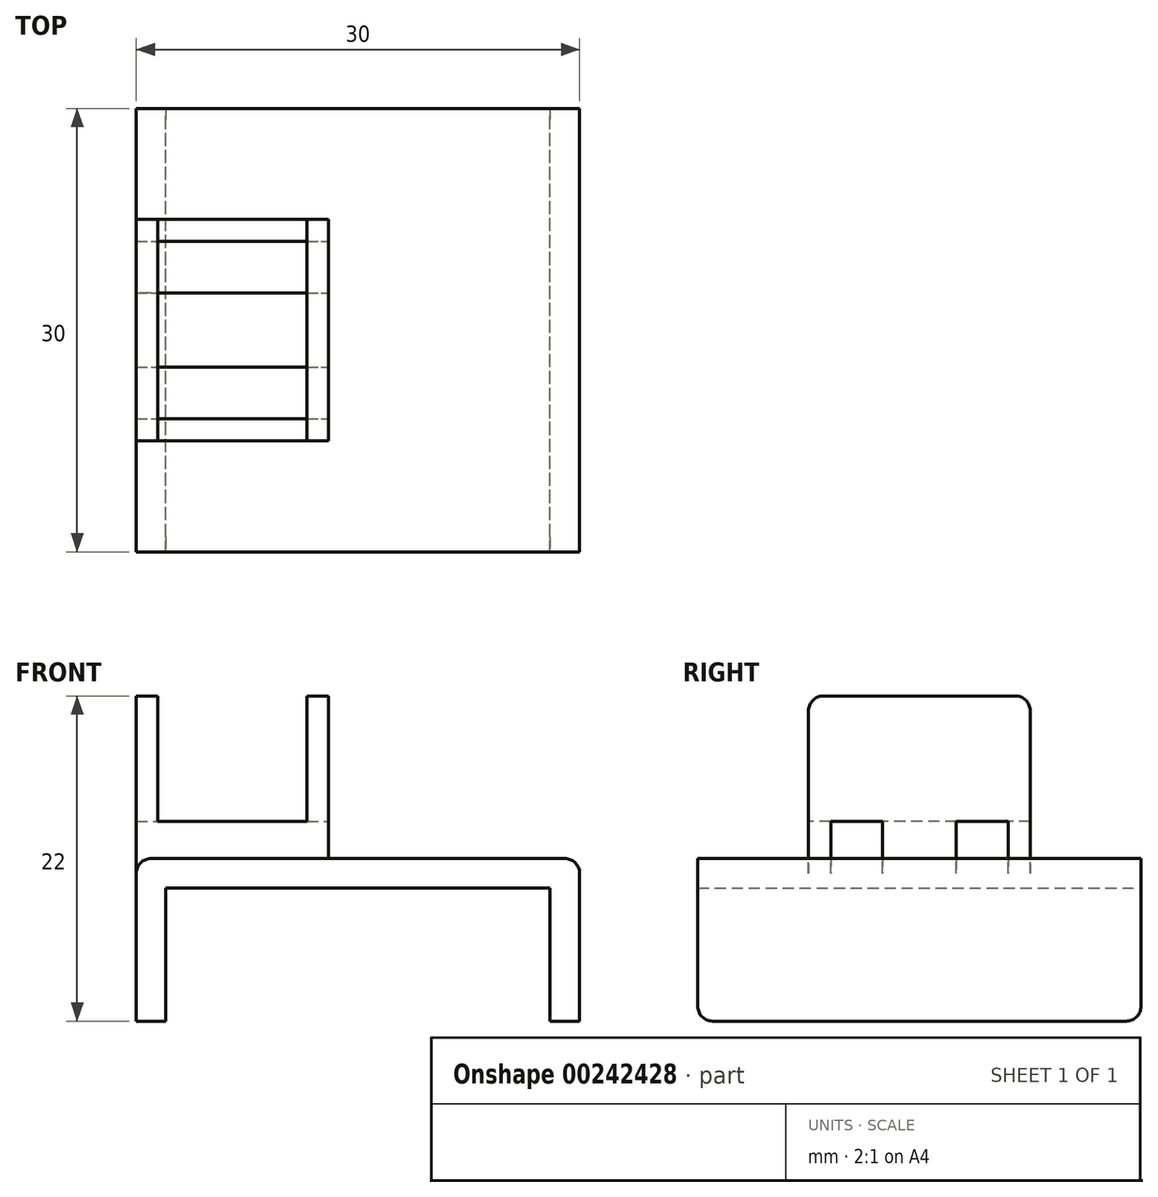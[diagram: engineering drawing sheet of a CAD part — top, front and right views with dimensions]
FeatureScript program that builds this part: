
annotation { "Feature Type Name" : "Feature", "Feature Type Description" : "" }
export const myFeature = defineFeature(function(context is Context, id is Id, definition is map)
    precondition{}
    {
        {
            var Q0;
            Q0=qCreatedBy(makeId("Top.planeOp"),FACE);
            var sketch = newSketch(context, id + "F0", { "sketchPlane" : qUnion([Q0])});
            skLineSegment(sketch, "E0.bottom", {"start": v(15, -15) * mm, "end": v(-15, -15) * mm});
            skLineSegment(sketch, "E0.top", {"start": v(15, 15) * mm, "end": v(-15, 15) * mm});
            skLineSegment(sketch, "E0.left", {"start": v(15, -15) * mm, "end": v(15, 15) * mm});
            skLineSegment(sketch, "E0.right", {"start": v(-15, -15) * mm, "end": v(-15, 15) * mm});
            skPoint(sketch, "E0.middle", {"position": v(0, 0) * mm});
            skSolve(sketch);
        }
        {
            var Q0;
            Q0=makeQuery(id+"F0.imprint","IMPRINT",FACE,{"disambiguationData":[TD([[makeQuery(id+"F0.imprint","IMPRINT",EDGE,{"derivedFrom":sQuery(id+"F0.wireOp",EDGE,"E0.bottom")}),-1.0]])]});
            extrude(context, id + "F1", {"entities" : qUnion([Q0]), "depth" : 11 * mm, "offsetDistance" : 25 * mm});
        }
        {
            var Q0;
            Q0=makeQuery(id+"F1.opExtrude","CAP_FACE",FACE,{"disambiguationData":[OSD([sQuery(id+"F0.wireOp",EDGE,"E0.bottom"),sQuery(id+"F0.wireOp",EDGE,"E0.top"),sQuery(id+"F0.wireOp",EDGE,"E0.left"),sQuery(id+"F0.wireOp",EDGE,"E0.right")])],"isStart":true});
            var sketch = newSketch(context, id + "F2", { "sketchPlane" : qUnion([Q0])});
            skLineSegment(sketch, "E1", {"start": v(-13, 15) * mm, "end": v(-13, -15) * mm});
            skLineSegment(sketch, "E2", {"start": v(13, 15) * mm, "end": v(13, -15) * mm});
            skLineSegment(sketch, "E3", {"start": v(0, -19.21) * mm, "end": v(0, -15) * mm, "construction": true});
            skSolve(sketch);
        }
        {
            var Q0;
            {var subQ0=sQuery(id+"F2.wireOp",EDGE,"E1");Q0=makeQuery(id+"F2.imprint","IMPRINT",FACE,{"disambiguationData":[TD([[makeQuery(id+"F2.imprint","IMPRINT",EDGE,{"derivedFrom":subQ0}),1.0]])]});}
            extrude(context, id + "F3", {"entities" : qUnion([Q0]), "operationType" : NewBodyOperationType.REMOVE, "oppositeDirection" : true, "depth" : 9 * mm, "offsetDistance" : 25 * mm});
        }
        {
            var Q0;
            Q0=makeQuery(id+"F1.opExtrude","CAP_FACE",FACE,{"disambiguationData":[OSD([sQuery(id+"F0.wireOp",EDGE,"E0.bottom"),sQuery(id+"F0.wireOp",EDGE,"E0.top"),sQuery(id+"F0.wireOp",EDGE,"E0.left"),sQuery(id+"F0.wireOp",EDGE,"E0.right")])],"isStart":false});
            var sketch = newSketch(context, id + "F4", { "sketchPlane" : qUnion([Q0])});
            skLineSegment(sketch, "E4", {"start": v(-2, 15) * mm, "end": v(-2, -15) * mm});
            skLineSegment(sketch, "E5", {"start": v(-13.55, 15) * mm, "end": v(-13.55, -15) * mm});
            skLineSegment(sketch, "E6", {"start": v(-3.45, 15) * mm, "end": v(-3.45, -15) * mm});
            skLineSegment(sketch, "E7", {"start": v(-15, 7.5) * mm, "end": v(-13.55, 7.5) * mm});
            skLineSegment(sketch, "E8", {"start": v(-15, -7.5) * mm, "end": v(-13.55, -7.5) * mm});
            skLineSegment(sketch, "E9", {"start": v(-3.45, 7.5) * mm, "end": v(-2, 7.5) * mm});
            skLineSegment(sketch, "E10", {"start": v(-3.45, -7.5) * mm, "end": v(-2, -7.5) * mm});
            skLineSegment(sketch, "E11", {"start": v(-15, 0) * mm, "end": v(-7.7, 0) * mm, "construction": true});
            skSolve(sketch);
        }
        {
            var Q0;
            {var subQ0=sQuery(id+"F4.wireOp",EDGE,"E7");Q0=makeQuery(id+"F4.imprint","IMPRINT",FACE,{"disambiguationData":[TD([[makeQuery(id+"F4.imprint","IMPRINT",EDGE,{"derivedFrom":subQ0}),-1.0]])]});}
            var Q1;
            {var subQ0=sQuery(id+"F4.wireOp",EDGE,"E9");Q1=makeQuery(id+"F4.imprint","IMPRINT",FACE,{"disambiguationData":[TD([[makeQuery(id+"F4.imprint","IMPRINT",EDGE,{"derivedFrom":subQ0}),-1.0]])]});}
            extrude(context, id + "F5", {"entities" : qUnion([Q0, Q1]), "operationType" : NewBodyOperationType.ADD, "depth" : 11 * mm, "offsetDistance" : 25 * mm});
        }
        {
            var Q0;
            Q0=makeQuery(id+"F1.opExtrude","CAP_FACE",FACE,{"disambiguationData":[OSD([sQuery(id+"F0.wireOp",EDGE,"E0.bottom"),sQuery(id+"F0.wireOp",EDGE,"E0.top"),sQuery(id+"F0.wireOp",EDGE,"E0.left"),sQuery(id+"F0.wireOp",EDGE,"E0.right")])],"isStart":false});
            var sketch = newSketch(context, id + "F6", { "sketchPlane" : qUnion([Q0])});
            skLineSegment(sketch, "E12", {"start": v(-13.55, 7.5) * mm, "end": v(-3.45, 7.5) * mm});
            skLineSegment(sketch, "E13", {"start": v(-13.55, -7.5) * mm, "end": v(-3.45, -7.5) * mm});
            skSolve(sketch);
        }
        {
            var Q0;
            Q0=makeQuery(id+"F6.imprint","IMPRINT",FACE,{"disambiguationData":[TD([[makeQuery(id+"F6.imprint","IMPRINT",EDGE,{"derivedFrom":sQuery(id+"F6.wireOp",EDGE,"E12")}),-1.0]])]});
            extrude(context, id + "F7", {"entities" : qUnion([Q0]), "operationType" : NewBodyOperationType.ADD, "depth" : 2.5 * mm, "offsetDistance" : 25 * mm});
        }
        {
            var Q0;
            Q0=makeQuery(id+"F5.opExtrude","SWEPT_FACE",FACE,{"disambiguationData":[OSD([sQuery(id+"F4.wireOp",EDGE,"E4")])]});
            var sketch = newSketch(context, id + "F8", { "sketchPlane" : qUnion([Q0])});
            skLineSegment(sketch, "E14.bottom", {"start": v(6, 13.5) * mm, "end": v(2.5, 13.5) * mm});
            skLineSegment(sketch, "E14.top", {"start": v(6, 11) * mm, "end": v(2.5, 11) * mm});
            skLineSegment(sketch, "E14.left", {"start": v(6, 11) * mm, "end": v(6, 13.5) * mm});
            skLineSegment(sketch, "E14.right", {"start": v(2.5, 13.5) * mm, "end": v(2.5, 11) * mm});
            skPoint(sketch, "E14.middle", {"position": v(4.25, 12.25) * mm});
            skLineSegment(sketch, "E15.bottom", {"start": v(-2.5, 11) * mm, "end": v(-6, 11) * mm});
            skLineSegment(sketch, "E15.top", {"start": v(-2.5, 13.5) * mm, "end": v(-6, 13.5) * mm});
            skLineSegment(sketch, "E15.left", {"start": v(-2.5, 11) * mm, "end": v(-2.5, 13.5) * mm});
            skLineSegment(sketch, "E15.right", {"start": v(-6, 11) * mm, "end": v(-6, 13.5) * mm});
            skPoint(sketch, "E15.middle", {"position": v(-4.25, 12.25) * mm});
            skLineSegment(sketch, "E16", {"start": v(0, 11) * mm, "end": v(0, 18.6) * mm, "construction": true});
            skSolve(sketch);
        }
        {
            var Q0;
            Q0=makeQuery(id+"F8.imprint","IMPRINT",FACE,{"disambiguationData":[TD([[makeQuery(id+"F8.imprint","IMPRINT",EDGE,{"derivedFrom":sQuery(id+"F8.wireOp",EDGE,"E15.bottom")}),-1.0]])]});
            var Q1;
            Q1=makeQuery(id+"F8.imprint","IMPRINT",FACE,{"disambiguationData":[TD([[makeQuery(id+"F8.imprint","IMPRINT",EDGE,{"derivedFrom":sQuery(id+"F8.wireOp",EDGE,"E14.bottom")}),1.0]])]});
            extrude(context, id + "F9", {"entities" : qUnion([Q0, Q1]), "operationType" : NewBodyOperationType.REMOVE, "endBound" : BoundingType.THROUGH_ALL, "oppositeDirection" : true, "depth" : 25 * mm, "offsetDistance" : 25 * mm});
        }
        {
            var Q0;
            Q0=makeQuery(id+"F5.opExtrude","CAP_EDGE",EDGE,{"disambiguationData":[OSD([sQuery(id+"F4.wireOp",EDGE,"E7")])],"isStart":false});
            var Q1;
            Q1=makeQuery(id+"F5.opExtrude","CAP_EDGE",EDGE,{"disambiguationData":[OSD([sQuery(id+"F4.wireOp",EDGE,"E8")])],"isStart":false});
            var Q2;
            Q2=makeQuery(id+"F5.opExtrude","CAP_EDGE",EDGE,{"disambiguationData":[OSD([sQuery(id+"F4.wireOp",EDGE,"E10")])],"isStart":false});
            var Q3;
            Q3=makeQuery(id+"F5.opExtrude","CAP_EDGE",EDGE,{"disambiguationData":[OSD([sQuery(id+"F4.wireOp",EDGE,"E9")])],"isStart":false});
            var Q4;
            {var subQ0=sQuery(id+"F0.wireOp",EDGE,"E0.right");var subQ1=sQuery(id+"F0.wireOp",EDGE,"E0.bottom");Q4=makeQuery(id+"F5.boolean.opBoolean","SPLIT",EDGE,{"disambiguationData":[TD([makeQuery(id+"F1.opExtrude","SWEPT_FACE",FACE,{"disambiguationData":[OSD([subQ1])]})])],"derivedFrom":makeQuery(id+"F1.opExtrude","CAP_EDGE",EDGE,{"disambiguationData":[OSD([subQ0])],"isStart":false})});}
            var Q5;
            Q5=makeQuery(id+"F1.opExtrude","CAP_EDGE",EDGE,{"disambiguationData":[OSD([sQuery(id+"F0.wireOp",EDGE,"E0.left")])],"isStart":false});
            var Q6;
            {var subQ0=sQuery(id+"F0.wireOp",EDGE,"E0.bottom");var subQ1=sQuery(id+"F0.wireOp",EDGE,"E0.right");Q6=makeQuery(id+"F3.boolean.opBoolean","SPLIT",EDGE,{"disambiguationData":[TD([makeQuery(id+"F1.opExtrude","SWEPT_FACE",FACE,{"disambiguationData":[OSD([subQ1])]})])],"derivedFrom":makeQuery(id+"F1.opExtrude","CAP_EDGE",EDGE,{"disambiguationData":[OSD([subQ0])],"isStart":true})});}
            var Q7;
            {var subQ0=sQuery(id+"F0.wireOp",EDGE,"E0.bottom");var subQ1=sQuery(id+"F0.wireOp",EDGE,"E0.left");Q7=makeQuery(id+"F3.boolean.opBoolean","SPLIT",EDGE,{"disambiguationData":[TD([makeQuery(id+"F1.opExtrude","SWEPT_FACE",FACE,{"disambiguationData":[OSD([subQ1])]})])],"derivedFrom":makeQuery(id+"F1.opExtrude","CAP_EDGE",EDGE,{"disambiguationData":[OSD([subQ0])],"isStart":true})});}
            var Q8;
            {var subQ0=sQuery(id+"F0.wireOp",EDGE,"E0.left");var subQ1=sQuery(id+"F0.wireOp",EDGE,"E0.top");Q8=makeQuery(id+"F3.boolean.opBoolean","SPLIT",EDGE,{"disambiguationData":[TD([makeQuery(id+"F1.opExtrude","SWEPT_FACE",FACE,{"disambiguationData":[OSD([subQ0])]})])],"derivedFrom":makeQuery(id+"F1.opExtrude","CAP_EDGE",EDGE,{"disambiguationData":[OSD([subQ1])],"isStart":true})});}
            var Q9;
            {var subQ0=sQuery(id+"F0.wireOp",EDGE,"E0.right");var subQ1=sQuery(id+"F0.wireOp",EDGE,"E0.top");Q9=makeQuery(id+"F3.boolean.opBoolean","SPLIT",EDGE,{"disambiguationData":[TD([makeQuery(id+"F1.opExtrude","SWEPT_FACE",FACE,{"disambiguationData":[OSD([subQ0])]})])],"derivedFrom":makeQuery(id+"F1.opExtrude","CAP_EDGE",EDGE,{"disambiguationData":[OSD([subQ1])],"isStart":true})});}
            var Q10;
            {var subQ0=sQuery(id+"F0.wireOp",EDGE,"E0.right");var subQ1=sQuery(id+"F0.wireOp",EDGE,"E0.top");Q10=makeQuery(id+"F5.boolean.opBoolean","SPLIT",EDGE,{"disambiguationData":[TD([makeQuery(id+"F1.opExtrude","SWEPT_FACE",FACE,{"disambiguationData":[OSD([subQ1])]})])],"derivedFrom":makeQuery(id+"F1.opExtrude","CAP_EDGE",EDGE,{"disambiguationData":[OSD([subQ0])],"isStart":false})});}
            var Q11;
            {var subQ0=sQuery(id+"F0.wireOp",EDGE,"E0.right");Q11=makeQuery(id+"F9.boolean.opBoolean","INTERSECT",EDGE,{"derivedFrom":[makeQuery(id+"F5.boolean.opBoolean","MERGE",FACE,{"derivedFrom":[makeQuery(id+"F1.opExtrude","SWEPT_FACE",FACE,{"disambiguationData":[OSD([subQ0])]}),makeQuery(id+"F5.opExtrude","SWEPT_FACE",FACE,{"disambiguationData":[OSD([subQ0])]})]}),makeQuery(id+"F9.opExtrude","SWEPT_FACE",FACE,{"disambiguationData":[OSD([sQuery(id+"F8.wireOp",EDGE,"E14.top")])]})]});}
            var Q12;
            {var subQ0=sQuery(id+"F0.wireOp",EDGE,"E0.right");Q12=makeQuery(id+"F9.boolean.opBoolean","INTERSECT",EDGE,{"derivedFrom":[makeQuery(id+"F5.boolean.opBoolean","MERGE",FACE,{"derivedFrom":[makeQuery(id+"F1.opExtrude","SWEPT_FACE",FACE,{"disambiguationData":[OSD([subQ0])]}),makeQuery(id+"F5.opExtrude","SWEPT_FACE",FACE,{"disambiguationData":[OSD([subQ0])]})]}),makeQuery(id+"F9.opExtrude","SWEPT_FACE",FACE,{"disambiguationData":[OSD([sQuery(id+"F8.wireOp",EDGE,"E15.bottom")])]})]});}
            fillet(context, id + "F10", {"entities" : qUnion([Q0, Q1, Q2, Q3, Q4, Q5, Q6, Q7, Q8, Q9, Q10, Q11, Q12]), "radius" : 1 * mm, "tangentPropagation" : true, "allowEdgeOverflow" : false});
        }
    });
